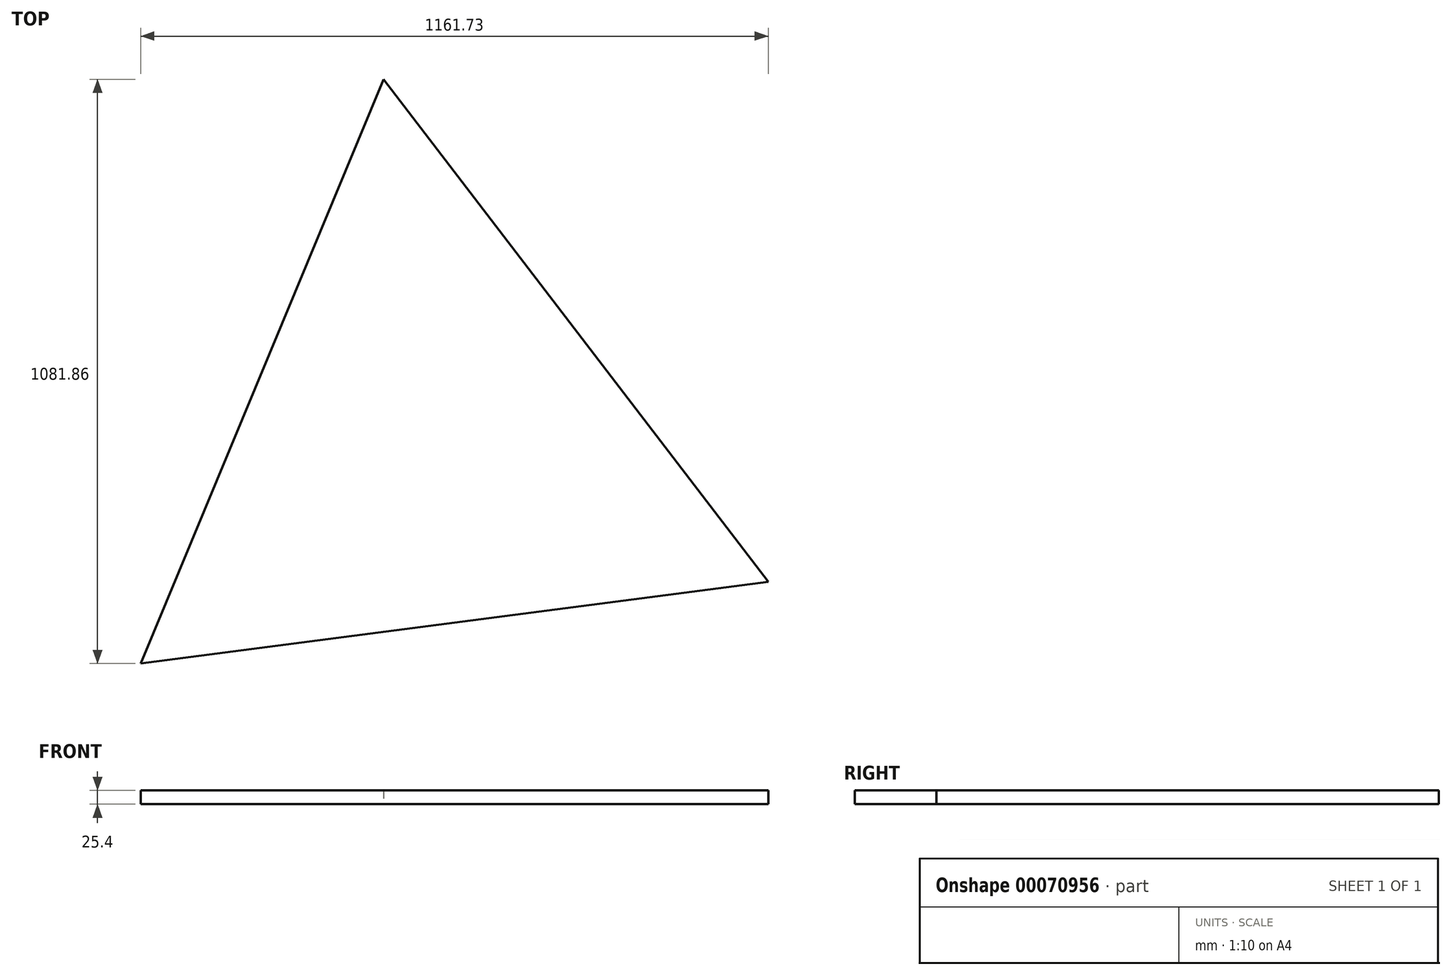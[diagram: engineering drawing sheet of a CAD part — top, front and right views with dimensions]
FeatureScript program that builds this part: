
annotation { "Feature Type Name" : "Feature", "Feature Type Description" : "" }
export const myFeature = defineFeature(function(context is Context, id is Id, definition is map)
    precondition{}
    {
        {
            var Q0;
            Q0=qCreatedBy(makeId("Top.planeOp"),FACE);
            var sketch = newSketch(context, id + "F0", { "sketchPlane" : qUnion([Q0])});
            skCircle(sketch, "E0.cCircle", {"center": v(0, 0) * mm, "radius": 338.2 * mm, "construction": true});
            skLineSegment(sketch, "E0.0", {"start": v(-87.49, 670.73) * mm, "end": v(624.61, -259.6) * mm});
            skLineSegment(sketch, "E0.1", {"start": v(624.61, -259.6) * mm, "end": v(-537.12, -411.13) * mm});
            skLineSegment(sketch, "E0.2", {"start": v(-537.12, -411.13) * mm, "end": v(-87.49, 670.73) * mm});
            skPoint(sketch, "E0.0.midPoint", {"position": v(268.56, 205.56) * mm});
            skSolve(sketch);
        }
        {
            var Q0;
            Q0=makeQuery(id+"F0.imprint","IMPRINT",FACE,{"disambiguationData":[TD([[makeQuery(id+"F0.imprint","IMPRINT",EDGE,{"derivedFrom":sQuery(id+"F0.wireOp",EDGE,"E0.0")}),-1.0]])]});
            extrude(context, id + "F1", {"entities" : qUnion([Q0]), "depth" : 25.4 * mm});
        }
    });
